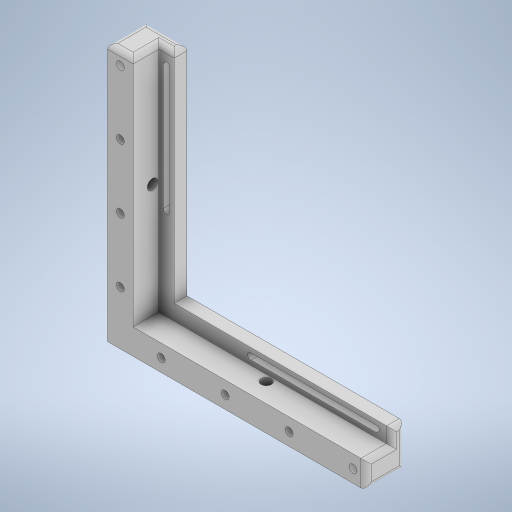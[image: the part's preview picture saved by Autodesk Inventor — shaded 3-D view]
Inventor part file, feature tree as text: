
AUTODESK INVENTOR PART (.ipt)
format: ipt  version: 2024 (Build 280153000, 153)  size: 374,272 bytes
history: native  units: mm
features: extrude x5, sketch x5, projected_geometry x5, fillet x1
ambient origin geometry x8: Origin, YZ Plane, XZ Plane, XY Plane, X Axis, Y Axis, Z Axis, Center Point
bodies: Solid1 (feature_tree)
feature tree (16):
  extrude  "Extrusion1"  Depth=10.0mm
  extrude  "Extrusion2"  Depth=101.0mm
  extrude  "Extrusion3"  Depth=5.0mm TaperAngle=0.0deg
  fillet  "Fillet1"  Radius=10.0mm
  extrude  "Extrusion4"  Depth=10.0mm TaperAngle=0.0deg
  extrude  "Extrusion5"  Depth=5.0mm
  sketch  "Sketch1"  dims[d0=101.0mm d1=10.0mm]
  sketch  "Sketch2"  dims[d2=6.0mm d3=101.0mm]
  projected_geometry  "Projected Loop1"
  sketch  "Sketch3"  dims[d4=16.0mm d5=5.0mm d6=0.0mm d7=10.0mm]
  projected_geometry  "Projected Loop2"
  projected_geometry  "Projected Loop3"
  sketch  "Sketch5"  dims[d8=10.0mm d9=10.0mm d10=0.0mm]
  projected_geometry  "Projected Loop5"
  sketch  "Sketch6"  dims[d11=5.0mm d12=5.0mm d13=85.0mm d14=5.0mm d15=5.0mm d16=5.0mm d17=5.0mm d18=25.0mm d19=25.0mm d20=25.0mm d21=25.0mm d22=3.0mm d23=3.0mm d24=3.0mm d25=3.0mm d26=3.0mm d27=3.0mm d28=3.0mm d29=3.0mm d30=16.0mm d31=0.0mm d32=3.0mm d34=3.0mm d35=30.0mm d36=6.0mm d37=6.0mm d38=2.5mm d39=2.5mm d40=2.5mm d41=30.0mm d42=2.5mm d43=2.0mm d47=25.0mm d48=25.0mm d49=10.0mm d50=89.0mm d51=4.0mm d52=2.5mm d53=44.5mm d54=4.0mm d55=10.0mm d56=0.0mm d57=2.5mm d58=44.5mm d59=4.0mm d60=10.0mm d61=0.0mm]
  projected_geometry  "Projected Loop6"
